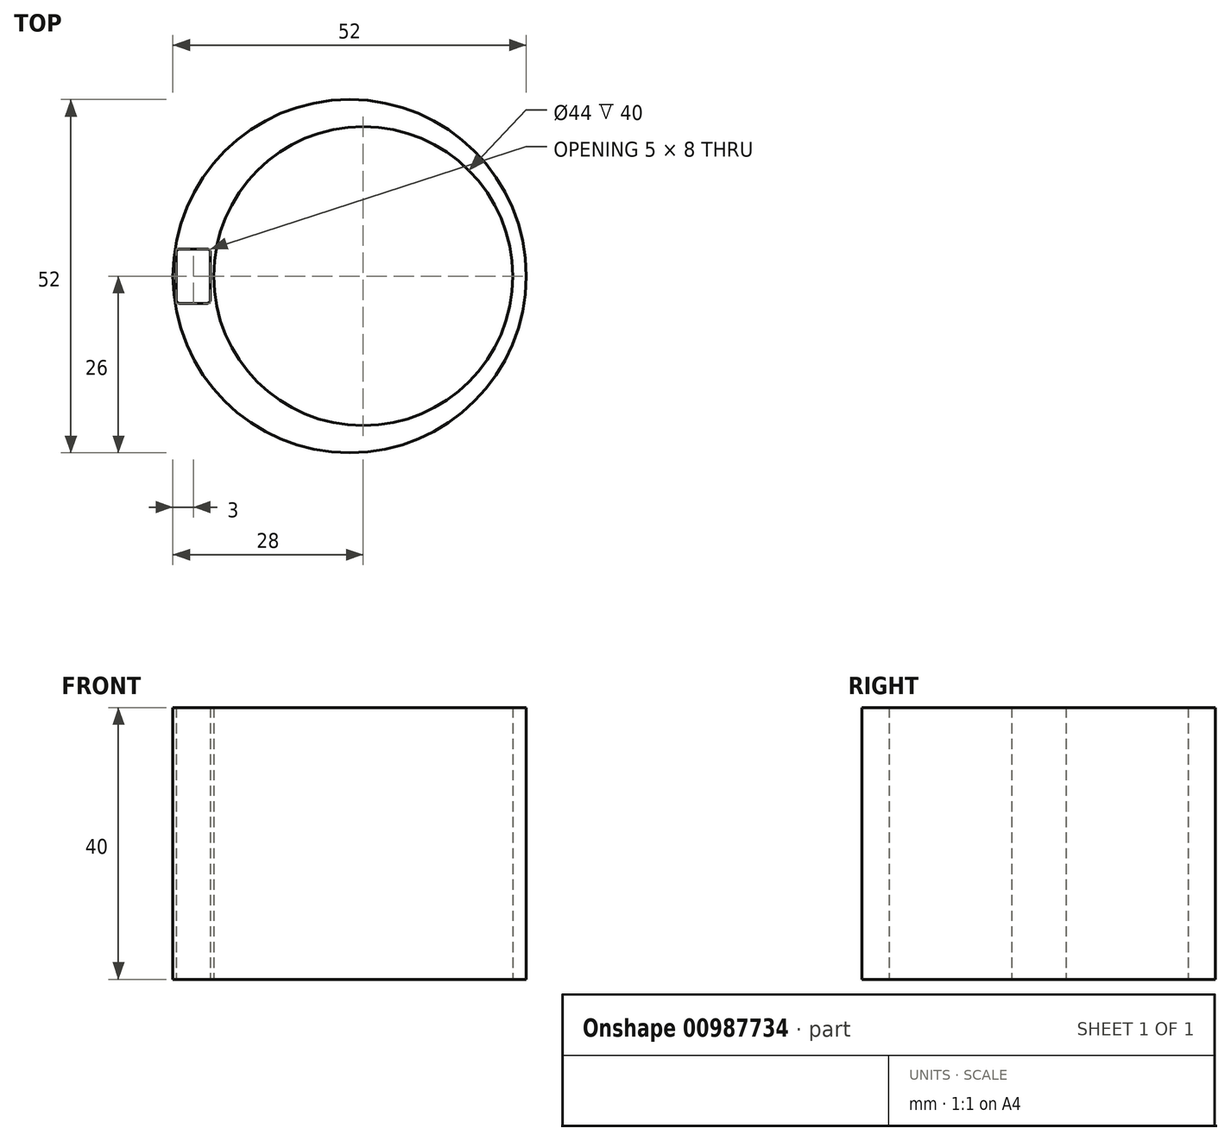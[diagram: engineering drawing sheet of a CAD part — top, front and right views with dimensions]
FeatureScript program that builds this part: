
annotation { "Feature Type Name" : "Feature", "Feature Type Description" : "" }
export const myFeature = defineFeature(function(context is Context, id is Id, definition is map)
    precondition{}
    {
        {
            var Q0;
            Q0=qCreatedBy(makeId("Top.planeOp"),FACE);
            var sketch = newSketch(context, id + "F0", { "sketchPlane" : qUnion([Q0])});
            skCircle(sketch, "E0", {"center": v(0, 0) * mm, "radius": 30 * mm});
            skCircle(sketch, "E1", {"center": v(0, 0) * mm, "radius": 26 * mm});
            skCircle(sketch, "E2", {"center": v(2, 0) * mm, "radius": 22 * mm});
            skLineSegment(sketch, "E3.bottom", {"start": v(-21, -4) * mm, "end": v(-25, -4) * mm});
            skLineSegment(sketch, "E3.top", {"start": v(-21, 4) * mm, "end": v(-25, 4) * mm});
            skLineSegment(sketch, "E3.left", {"start": v(-20.5, -3.5) * mm, "end": v(-20.5, 3.5) * mm});
            skLineSegment(sketch, "E3.right", {"start": v(-25.5, -3.5) * mm, "end": v(-25.5, 3.5) * mm});
            skPoint(sketch, "E3.middle", {"position": v(-23, 0) * mm});
            skPoint(sketch, "E4.visualSharp", {"position": v(-25.5, 4) * mm});
            skArc(sketch, "E4.filletArc", {"start": v(-25, 4) * mm, "mid": v(-25.35, 3.85) * mm, "end": v(-25.5, 3.5) * mm});
            skPoint(sketch, "E5.visualSharp", {"position": v(-20.5, 4) * mm});
            skArc(sketch, "E5.filletArc", {"start": v(-20.5, 3.5) * mm, "mid": v(-20.65, 3.85) * mm, "end": v(-21, 4) * mm});
            skPoint(sketch, "E6.visualSharp", {"position": v(-20.5, -4) * mm});
            skArc(sketch, "E6.filletArc", {"start": v(-21, -4) * mm, "mid": v(-20.65, -3.85) * mm, "end": v(-20.5, -3.5) * mm});
            skPoint(sketch, "E7.visualSharp", {"position": v(-25.5, -4) * mm});
            skArc(sketch, "E7.filletArc", {"start": v(-25.5, -3.5) * mm, "mid": v(-25.35, -3.85) * mm, "end": v(-25, -4) * mm});
            skSolve(sketch);
        }
        {
            var Q0;
            Q0=makeQuery(id+"F0.imprint","IMPRINT",FACE,{"disambiguationData":[TD([[makeQuery(id+"F0.imprint","IMPRINT",EDGE,{"derivedFrom":sQuery(id+"F0.wireOp",EDGE,"E1")}),1.0]])]});
            extrude(context, id + "F1", {"entities" : qUnion([Q0]), "depth" : 40 * mm, "offsetDistance" : 25 * mm});
        }
    });
